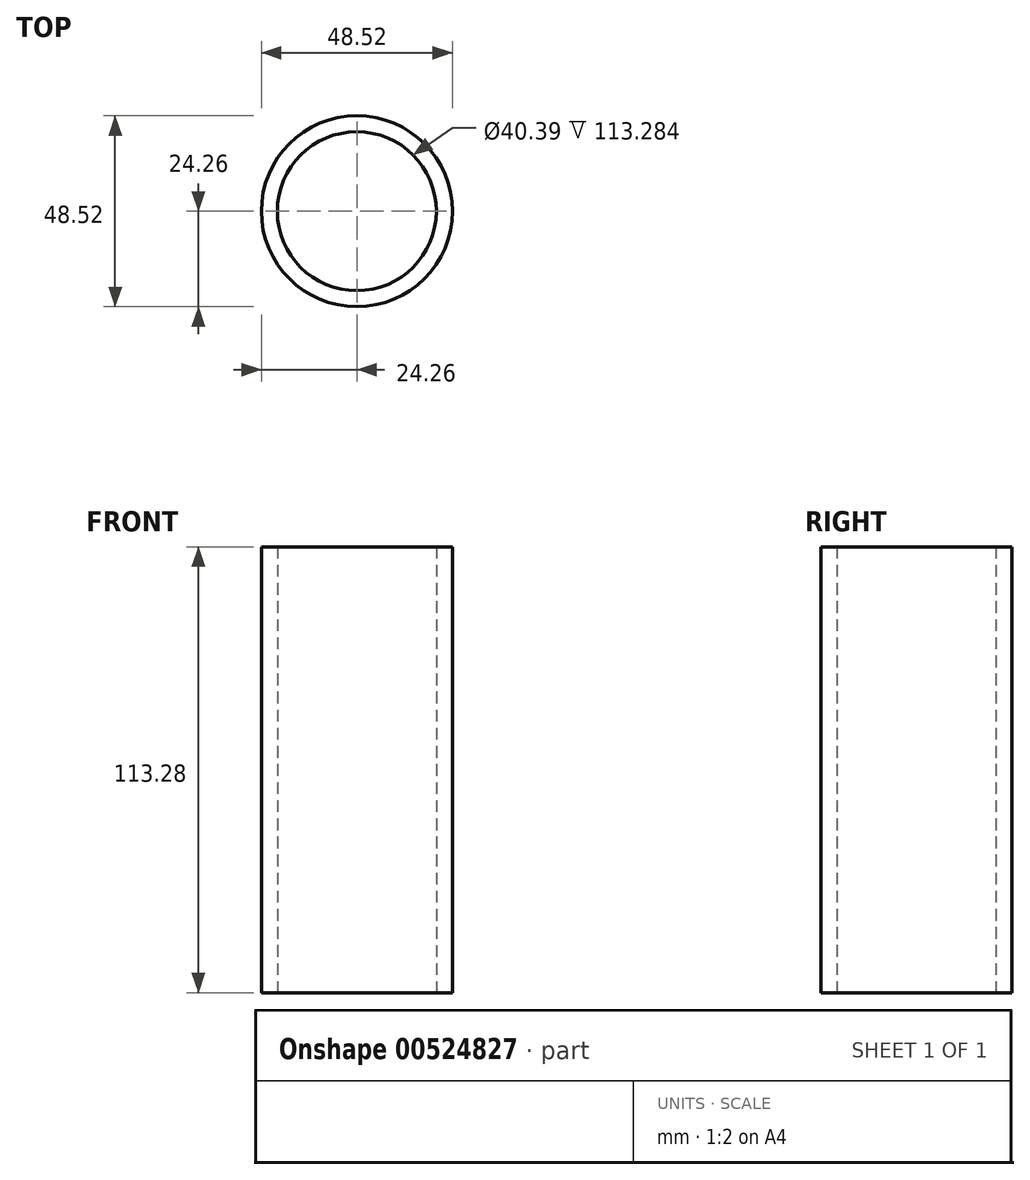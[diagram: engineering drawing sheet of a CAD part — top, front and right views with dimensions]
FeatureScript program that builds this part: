
annotation { "Feature Type Name" : "Feature", "Feature Type Description" : "" }
export const myFeature = defineFeature(function(context is Context, id is Id, definition is map)
    precondition{}
    {
        {
            var Q0;
            Q0=qCreatedBy(makeId("Top.planeOp"),FACE);
            var sketch = newSketch(context, id + "F0", { "sketchPlane" : qUnion([Q0])});
            skCircle(sketch, "E0", {"center": v(0, 0) * mm, "radius": 24.26 * mm});
            skCircle(sketch, "E1", {"center": v(0, 0) * mm, "radius": 20.2 * mm});
            skSolve(sketch);
        }
        {
            var Q0;
            Q0 = qSketchRegion(id + "F0", true);
            extrude(context, id + "F1", {"entities" : qUnion([Q0]), "depth" : 113.28 * mm, "offsetDistance" : 25.4 * mm});
        }
    });
